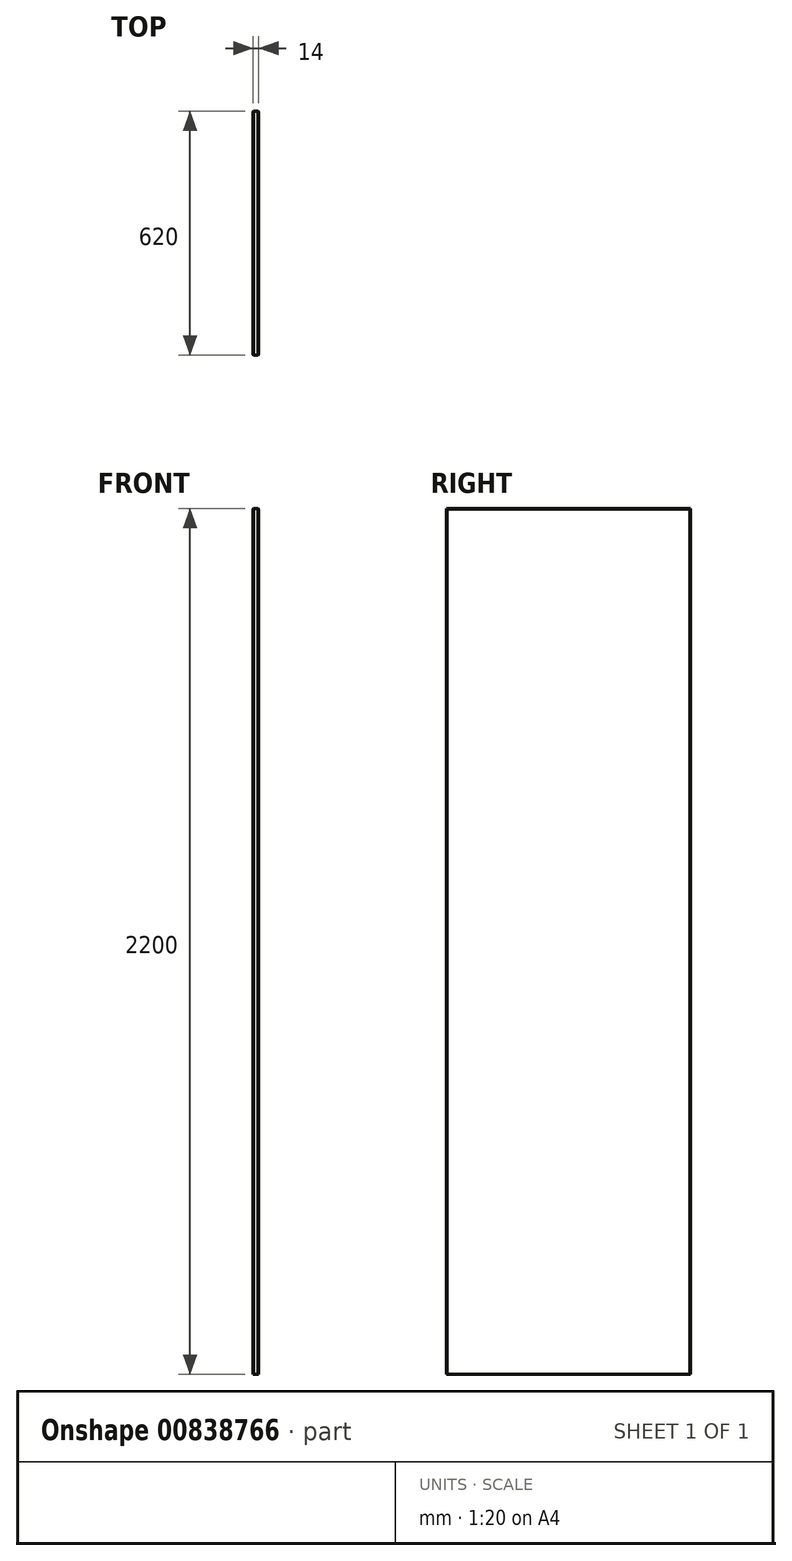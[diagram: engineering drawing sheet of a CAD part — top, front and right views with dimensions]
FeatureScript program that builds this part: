
annotation { "Feature Type Name" : "Feature", "Feature Type Description" : "" }
export const myFeature = defineFeature(function(context is Context, id is Id, definition is map)
    precondition{}
    {
        {
            var Q0;
            Q0=qCreatedBy(makeId("Right.planeOp"),FACE);
            var sketch = newSketch(context, id + "F0", { "sketchPlane" : qUnion([Q0])});
            skLineSegment(sketch, "E0.bottom", {"start": v(0, 0) * mm, "end": v(-50.65, 0) * mm});
            skLineSegment(sketch, "E0.top", {"start": v(0, 38.28) * mm, "end": v(-50.65, 38.28) * mm});
            skLineSegment(sketch, "E0.left", {"start": v(0, 0) * mm, "end": v(0, 38.28) * mm});
            skLineSegment(sketch, "E0.right", {"start": v(-50.65, 0) * mm, "end": v(-50.65, 38.28) * mm});
            skSolve(sketch);
        }
        {
            var Q0;
            Q0=makeQuery(id+"F0.imprint","IMPRINT",FACE,{"disambiguationData":[TD([[makeQuery(id+"F0.imprint","IMPRINT",EDGE,{"derivedFrom":sQuery(id+"F0.wireOp",EDGE,"E0.bottom")}),-1.0]])]});
            extrude(context, id + "F1", {"entities" : qUnion([Q0]), "oppositeDirection" : true, "depth" : 14 * mm, "offsetDistance" : 25.4 * mm});
        }
        {
            var Q0;
            Q0=makeQuery(id+"F1.opExtrude","SWEPT_FACE",FACE,{"disambiguationData":[OSD([sQuery(id+"F0.wireOp",EDGE,"E0.bottom")])]});
            extrude(context, id + "F2", {"entities" : qUnion([Q0]), "operationType" : NewBodyOperationType.ADD, "oppositeDirection" : true, "depth" : 2200 * mm, "offsetDistance" : 25.4 * mm});
        }
        {
            var Q0;
            {var subQ0=sQuery(id+"F0.wireOp",EDGE,"E0.left");Q0=makeQuery(id+"F2.boolean.opBoolean","MERGE",FACE,{"derivedFrom":[makeQuery(id+"F1.opExtrude","SWEPT_FACE",FACE,{"disambiguationData":[OSD([subQ0])]}),makeQuery(id+"F2.opExtrude","SWEPT_FACE",FACE,{"disambiguationData":[OSD([sQuery(id+"F0.wireOp",EDGE,"E0.bottom"),subQ0])]})]});}
            extrude(context, id + "F3", {"entities" : qUnion([Q0]), "operationType" : NewBodyOperationType.ADD, "oppositeDirection" : true, "depth" : 620 * mm, "offsetDistance" : 25 * mm});
        }
        {
            var Q0;
            {var subQ0=sQuery(id+"F0.wireOp",EDGE,"E0.left");var subQ1=sQuery(id+"F0.wireOp",EDGE,"E0.bottom");Q0=makeQuery(id+"F3.boolean.opBoolean","MERGE",FACE,{"derivedFrom":[makeQuery(id+"F2.boolean.opBoolean","MERGE",FACE,{"derivedFrom":[makeQuery(id+"F1.opExtrude","CAP_FACE",FACE,{"disambiguationData":[OSD([subQ1,sQuery(id+"F0.wireOp",EDGE,"E0.top"),subQ0,sQuery(id+"F0.wireOp",EDGE,"E0.right")])],"isStart":true}),makeQuery(id+"F2.opExtrude","SWEPT_FACE",FACE,{"disambiguationData":[OSD([subQ1]),TDD([makeQuery(id+"F1.opExtrude","CAP_EDGE",EDGE,{"disambiguationData":[OSD([subQ1])],"isStart":true})])]})]}),makeQuery(id+"F3.opExtrude","SWEPT_FACE",FACE,{"disambiguationData":[OSD([subQ1,subQ0]),TDD([makeQuery(id+"F2.boolean.opBoolean","MERGE",EDGE,{"derivedFrom":[makeQuery(id+"F1.opExtrude","CAP_EDGE",EDGE,{"disambiguationData":[OSD([subQ0])],"isStart":true}),makeQuery(id+"F2.opExtrude","SWEPT_EDGE",EDGE,{"disambiguationData":[OSD([subQ1,subQ0]),TDD([makeQuery(id+"F1.opExtrude","CAP_VERTEX",VERTEX,{"disambiguationData":[OSD([subQ1,subQ0])],"isStart":true})])]})]})])]})]});}
            var Q1;
            {var subQ0=sQuery(id+"F0.wireOp",EDGE,"E0.left");var subQ1=sQuery(id+"F0.wireOp",EDGE,"E0.bottom");Q1=makeQuery(id+"F3.boolean.opBoolean","MERGE",FACE,{"derivedFrom":[makeQuery(id+"F2.boolean.opBoolean","MERGE",FACE,{"derivedFrom":[makeQuery(id+"F1.opExtrude","CAP_FACE",FACE,{"disambiguationData":[OSD([subQ1,sQuery(id+"F0.wireOp",EDGE,"E0.top"),subQ0,sQuery(id+"F0.wireOp",EDGE,"E0.right")])],"isStart":false}),makeQuery(id+"F2.opExtrude","SWEPT_FACE",FACE,{"disambiguationData":[OSD([subQ1]),TDD([makeQuery(id+"F1.opExtrude","CAP_EDGE",EDGE,{"disambiguationData":[OSD([subQ1])],"isStart":false})])]})]}),makeQuery(id+"F3.opExtrude","SWEPT_FACE",FACE,{"disambiguationData":[OSD([subQ1,subQ0]),TDD([makeQuery(id+"F2.boolean.opBoolean","MERGE",EDGE,{"derivedFrom":[makeQuery(id+"F1.opExtrude","CAP_EDGE",EDGE,{"disambiguationData":[OSD([subQ0])],"isStart":false}),makeQuery(id+"F2.opExtrude","SWEPT_EDGE",EDGE,{"disambiguationData":[OSD([subQ1,subQ0]),TDD([makeQuery(id+"F1.opExtrude","CAP_VERTEX",VERTEX,{"disambiguationData":[OSD([subQ1,subQ0])],"isStart":false})])]})]})])]})]});}
            chamfer(context, id + "F4", {"entities" : qUnion([Q0, Q1]), "width" : 1 * mm, "tangentPropagation" : true});
        }
    });
